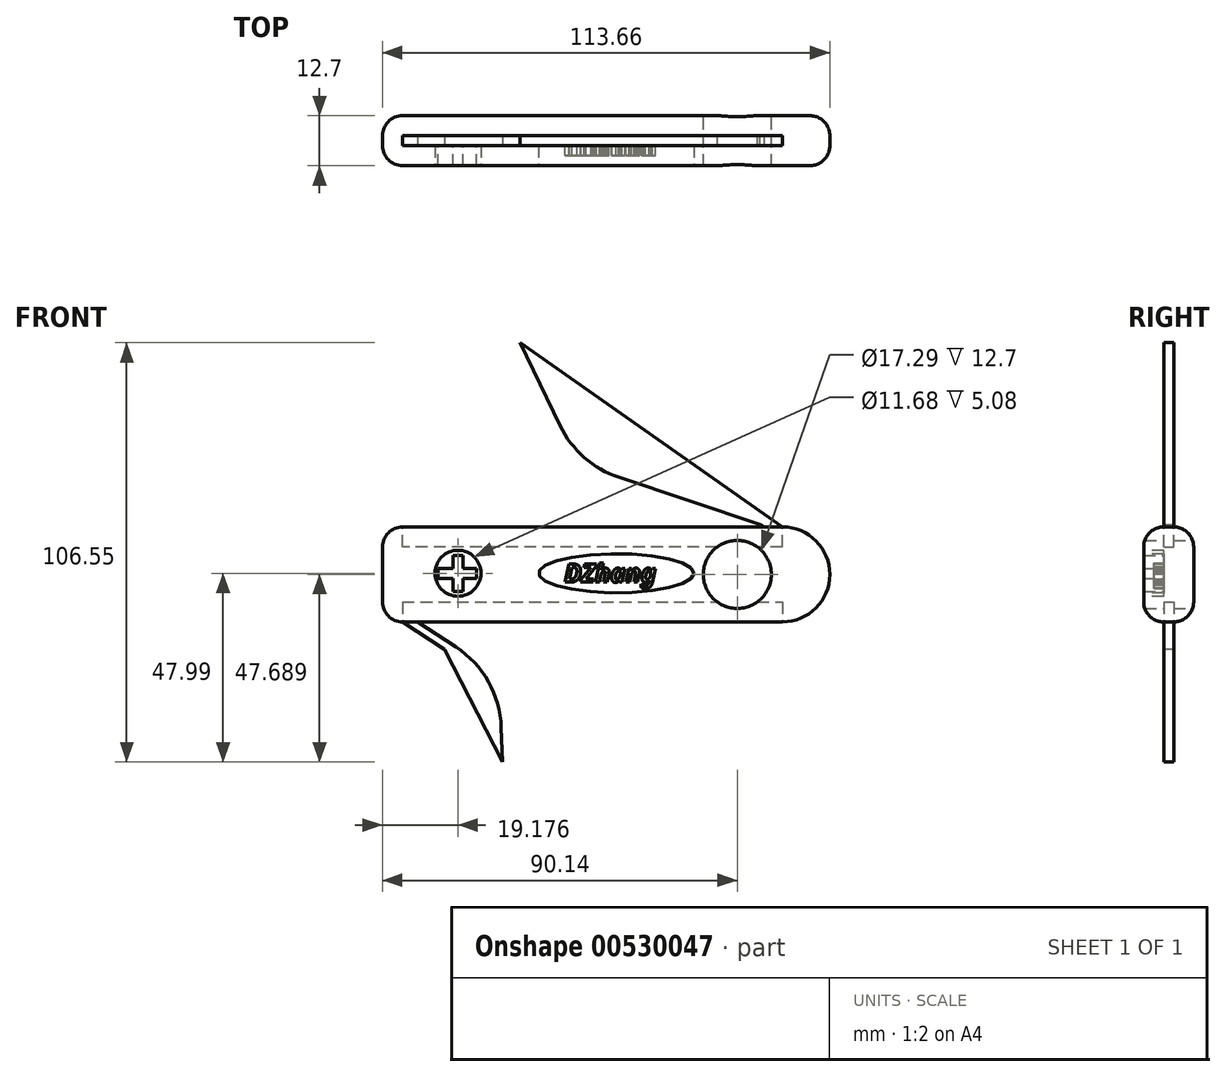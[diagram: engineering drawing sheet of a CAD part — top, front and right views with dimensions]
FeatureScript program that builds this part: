
annotation { "Feature Type Name" : "Feature", "Feature Type Description" : "" }
export const myFeature = defineFeature(function(context is Context, id is Id, definition is map)
    precondition{}
    {
        {
            var Q0;
            Q0=qCreatedBy(makeId("Front.planeOp"),FACE);
            var sketch = newSketch(context, id + "F0", { "sketchPlane" : qUnion([Q0])});
            skLineSegment(sketch, "E0", {"start": v(-34.28, 8.34) * mm, "end": v(23.42, 8.34) * mm});
            skLineSegment(sketch, "E1", {"start": v(23.42, 8.34) * mm, "end": v(23.42, -8.95) * mm, "construction": true});
            skLineSegment(sketch, "E2", {"start": v(23.42, -8.95) * mm, "end": v(-34.28, -8.95) * mm});
            skArc(sketch, "E3", {"start": v(23.42, -8.95) * mm, "mid": v(32.06, -0.3) * mm, "end": v(23.42, 8.34) * mm});
            skArc(sketch, "E4", {"start": v(23.42, 8.34) * mm, "mid": v(14.78, -0.3) * mm, "end": v(23.42, -8.95) * mm});
            skLineSegment(sketch, "E5", {"start": v(23.42, -8.95) * mm, "end": v(34.88, -8.95) * mm});
            skLineSegment(sketch, "E6", {"start": v(23.42, 8.34) * mm, "end": v(34.88, 8.34) * mm});
            skArc(sketch, "E7", {"start": v(34.88, -8.95) * mm, "mid": v(43.52, -0.3) * mm, "end": v(34.88, 8.34) * mm});
            skLineSegment(sketch, "E8", {"start": v(-66.72, -12.36) * mm, "end": v(34.88, -12.36) * mm});
            skLineSegment(sketch, "E9", {"start": v(34.88, -8.95) * mm, "end": v(34.88, -12.36) * mm, "construction": true});
            skLineSegment(sketch, "E10", {"start": v(34.88, 8.34) * mm, "end": v(34.88, 11.76) * mm, "construction": true});
            skLineSegment(sketch, "E11", {"start": v(34.88, 11.76) * mm, "end": v(-66.72, 11.76) * mm});
            skLineSegment(sketch, "E12", {"start": v(-66.72, -12.36) * mm, "end": v(-66.72, 11.76) * mm});
            skLineSegment(sketch, "E13", {"start": v(-34.28, -8.95) * mm, "end": v(-66.72, -8.95) * mm});
            skLineSegment(sketch, "E14", {"start": v(-34.28, 8.34) * mm, "end": v(-66.72, 8.34) * mm});
            skArc(sketch, "E15", {"start": v(34.88, -12.36) * mm, "mid": v(46.94, -0.3) * mm, "end": v(34.88, 11.76) * mm});
            skSolve(sketch);
        }
        {
            var Q0;
            {var subQ0=sQuery(id+"F0.wireOp",EDGE,"E0");Q0=makeQuery(id+"F0.imprint","IMPRINT",FACE,{"disambiguationData":[TD([[makeQuery(id+"F0.imprint","IMPRINT",EDGE,{"derivedFrom":subQ0}),-1.0]])]});}
            var Q1;
            {var subQ2=sQuery(id+"F0.wireOp",EDGE,"E0");Q1=makeQuery(id+"F0.imprint","IMPRINT",FACE,{"disambiguationData":[TD([[makeQuery(id+"F0.imprint","IMPRINT",EDGE,{"derivedFrom":subQ2}),1.0]])]});}
            var Q2;
            Q2=makeQuery(id+"F0.imprint","IMPRINT",FACE,{"disambiguationData":[TD([[makeQuery(id+"F0.imprint","IMPRINT",EDGE,{"derivedFrom":sQuery(id+"F0.wireOp",EDGE,"E3")}),-1.0]])]});
            extrude(context, id + "F1", {"entities" : qUnion([Q0, Q1, Q2]), "depth" : 12.7 * mm, "offsetDistance" : 25.4 * mm});
        }
        {
            var Q0;
            Q0=makeQuery(id+"F1.opExtrude","SWEPT_FACE",FACE,{"disambiguationData":[OSD([sQuery(id+"F0.wireOp",EDGE,"E8")])]});
            var Q1;
            Q1=makeQuery(id+"F1.opExtrude","SWEPT_FACE",FACE,{"disambiguationData":[OSD([sQuery(id+"F0.wireOp",EDGE,"E11")])]});
            fillet(context, id + "F2", {"entities" : qUnion([Q0, Q1]), "radius" : 5.08 * mm, "tangentPropagation" : true, "allowEdgeOverflow" : false});
        }
        {
            var Q0;
            Q0=makeQuery(id+"F1.opExtrude","SWEPT_FACE",FACE,{"disambiguationData":[OSD([sQuery(id+"F0.wireOp",EDGE,"E12")])]});
            fillet(context, id + "F3", {"entities" : qUnion([Q0]), "radius" : 5.08 * mm, "tangentPropagation" : true, "allowEdgeOverflow" : false});
        }
        {
            var Q0;
            Q0=makeQuery(id+"F1.opExtrude","SWEPT_FACE",FACE,{"disambiguationData":[OSD([sQuery(id+"F0.wireOp",EDGE,"E11")])]});
            extrude(context, id + "F4", {"entities" : qUnion([Q0]), "operationType" : NewBodyOperationType.REMOVE, "oppositeDirection" : true, "depth" : 5.08 * mm, "offsetDistance" : 25.4 * mm});
        }
        {
            var Q0;
            {var subQ0=sQuery(id+"F0.wireOp",EDGE,"E11");Q0=makeQuery(id+"F4.boolean.opBoolean","COPY",FACE,{"derivedFrom":makeQuery(id+"F4.opExtrude","SWEPT_FACE",FACE,{"disambiguationData":[OSD([subQ0]),TDD([makeQuery(id+"F2.opFillet","BLEND_EDGE",EDGE,{"blendedFrom":[makeQuery(id+"F1.opExtrude","CAP_EDGE",EDGE,{"disambiguationData":[OSD([subQ0])],"isStart":true}),makeQuery(id+"F1.opExtrude","SWEPT_FACE",FACE,{"disambiguationData":[OSD([subQ0])]})],"blendedInto":[makeQuery(id+"F1.opExtrude","SWEPT_FACE",FACE,{"disambiguationData":[OSD([subQ0])]})]})])]})});}
            var sketch = newSketch(context, id + "F5", { "sketchPlane" : qUnion([Q0])});
            skLineSegment(sketch, "E16", {"start": v(34.88, 11.76) * mm, "end": v(-31.74, 58.56) * mm});
            skLineSegment(sketch, "E17", {"start": v(-31.74, 58.56) * mm, "end": v(-21.58, 37.48) * mm});
            skLineSegment(sketch, "E18", {"start": v(34.88, 9.22) * mm, "end": v(29.21, 12.41) * mm});
            skPoint(sketch, "E19.visualSharp", {"position": v(-11.4, 16.33) * mm});
            skLineSegment(sketch, "E20", {"start": v(-6.74, 24.4) * mm, "end": v(29.21, 12.41) * mm});
            skPoint(sketch, "E21.visualSharp", {"position": v(-16.92, 27.8) * mm});
            skArc(sketch, "E21.filletArc", {"start": v(-21.58, 37.48) * mm, "mid": v(-15.48, 29.44) * mm, "end": v(-6.74, 24.4) * mm});
            skSolve(sketch);
        }
        {
            var Q0;
            {var subQ8=sQuery(id+"F5.wireOp",EDGE,"E16");Q0=makeQuery(id+"F5.imprint","IMPRINT",FACE,{"disambiguationData":[TD([[makeQuery(id+"F5.imprint","IMPRINT",EDGE,{"derivedFrom":subQ8}),1.0]])]});}
            extrude(context, id + "F6", {"entities" : qUnion([Q0]), "depth" : 2.54 * mm, "offsetDistance" : 25.4 * mm});
        }
        {
            var Q0;
            Q0=makeQuery(id+"F1.opExtrude","SWEPT_FACE",FACE,{"disambiguationData":[OSD([sQuery(id+"F0.wireOp",EDGE,"E8")])]});
            extrude(context, id + "F7", {"entities" : qUnion([Q0]), "operationType" : NewBodyOperationType.REMOVE, "oppositeDirection" : true, "depth" : 5.08 * mm, "offsetDistance" : 25.4 * mm});
        }
        {
            var Q0;
            Q0=makeQuery(id+"F2.opFillet","SPLIT",FACE,{"disambiguationData":[OD(1.0)],"derivedFrom":makeQuery(id+"F1.opExtrude","CAP_FACE",FACE,{"disambiguationData":[OSD([sQuery(id+"F0.wireOp",EDGE,"E3"),sQuery(id+"F0.wireOp",EDGE,"E4"),sQuery(id+"F0.wireOp",EDGE,"E8"),sQuery(id+"F0.wireOp",EDGE,"E11"),sQuery(id+"F0.wireOp",EDGE,"E12"),sQuery(id+"F0.wireOp",EDGE,"E15")])],"isStart":false})});
            var sketch = newSketch(context, id + "F8", { "sketchPlane" : qUnion([Q0])});
            skEllipse(sketch, "E22", {"center": v(-7.34, 0) * mm, "majorRadius": 19.7 * mm, "minorRadius": 4.96 * mm, "majorAxis": v(1, 0)});
            skCircle(sketch, "E23", {"center": v(-47.54, 0) * mm, "radius": 5.84 * mm});
            skSolve(sketch);
        }
        {
            var Q0;
            Q0=makeQuery(id+"F8.imprint","IMPRINT",FACE,{"disambiguationData":[TD([[makeQuery(id+"F8.imprint","IMPRINT",EDGE,{"derivedFrom":sQuery(id+"F8.wireOp",EDGE,"E22")}),1.0]])]});
            var Q1;
            Q1=makeQuery(id+"F8.imprint","IMPRINT",FACE,{"disambiguationData":[TD([[makeQuery(id+"F8.imprint","IMPRINT",EDGE,{"derivedFrom":sQuery(id+"F8.wireOp",EDGE,"E23")}),1.0]])]});
            extrude(context, id + "F9", {"entities" : qUnion([Q0, Q1]), "operationType" : NewBodyOperationType.REMOVE, "oppositeDirection" : true, "depth" : 5.08 * mm, "offsetDistance" : 25.4 * mm});
        }
        {
            var Q0;
            Q0=makeQuery(id+"F9.boolean.opBoolean","COPY",FACE,{"derivedFrom":makeQuery(id+"F9.opExtrude","CAP_FACE",FACE,{"disambiguationData":[OSD([sQuery(id+"F8.wireOp",EDGE,"E23")])],"isStart":false})});
            var sketch = newSketch(context, id + "F10", { "sketchPlane" : qUnion([Q0])});
            skLineSegment(sketch, "E24", {"start": v(-52.55, 0) * mm, "end": v(-52.55, -1.26) * mm});
            skLineSegment(sketch, "E25", {"start": v(-52.55, -1.26) * mm, "end": v(-42.86, -1.26) * mm});
            skLineSegment(sketch, "E26", {"start": v(-42.86, -1.26) * mm, "end": v(-42.86, 0) * mm});
            skLineSegment(sketch, "E27", {"start": v(-42.86, 0) * mm, "end": v(-42.86, 1.26) * mm});
            skLineSegment(sketch, "E28", {"start": v(-42.86, 1.26) * mm, "end": v(-52.55, 1.26) * mm});
            skLineSegment(sketch, "E29", {"start": v(-52.55, 1.26) * mm, "end": v(-52.55, 0) * mm});
            skLineSegment(sketch, "E30", {"start": v(-47.54, 4.56) * mm, "end": v(-46.28, 4.56) * mm});
            skLineSegment(sketch, "E31", {"start": v(-46.28, 4.56) * mm, "end": v(-46.28, 0) * mm});
            skLineSegment(sketch, "E32", {"start": v(-46.28, 0) * mm, "end": v(-46.28, -4.56) * mm});
            skLineSegment(sketch, "E33", {"start": v(-46.28, -4.56) * mm, "end": v(-47.54, -4.56) * mm});
            skLineSegment(sketch, "E34", {"start": v(-47.54, -4.56) * mm, "end": v(-48.8, -4.56) * mm});
            skLineSegment(sketch, "E35", {"start": v(-48.8, -4.56) * mm, "end": v(-48.8, 4.56) * mm});
            skLineSegment(sketch, "E36", {"start": v(-48.8, 4.56) * mm, "end": v(-47.54, 4.56) * mm});
            skSolve(sketch);
        }
        {
            var Q0;
            {var subQ4=sQuery(id+"F10.wireOp",EDGE,"E26");Q0=makeQuery(id+"F10.imprint","IMPRINT",FACE,{"disambiguationData":[TD([[makeQuery(id+"F10.imprint","IMPRINT",EDGE,{"derivedFrom":subQ4}),1.0]])]});}
            var Q1;
            {var subQ1=sQuery(id+"F10.wireOp",EDGE,"E33");Q1=makeQuery(id+"F10.imprint","IMPRINT",FACE,{"disambiguationData":[TD([[makeQuery(id+"F10.imprint","IMPRINT",EDGE,{"derivedFrom":subQ1}),-1.0]])]});}
            var Q2;
            {var subQ3=sQuery(id+"F10.wireOp",EDGE,"E25");var subQ5=sQuery(id+"F10.wireOp",EDGE,"E35");var subQ6=makeQuery(id+"F10.imprint","INTERSECT",VERTEX,{"derivedFrom":[subQ3,subQ5]});Q2=makeQuery(id+"F10.imprint","IMPRINT",FACE,{"disambiguationData":[TD([[makeQuery(id+"F10.imprint","IMPRINT",EDGE,{"disambiguationData":[TD([[subQ6,-1.0]])],"derivedFrom":subQ3}),1.0]])]});}
            var Q3;
            {var subQ5=sQuery(id+"F10.wireOp",EDGE,"E30");Q3=makeQuery(id+"F10.imprint","IMPRINT",FACE,{"disambiguationData":[TD([[makeQuery(id+"F10.imprint","IMPRINT",EDGE,{"derivedFrom":subQ5}),-1.0]])]});}
            var Q4;
            {var subQ5=sQuery(id+"F10.wireOp",EDGE,"E24");Q4=makeQuery(id+"F10.imprint","IMPRINT",FACE,{"disambiguationData":[TD([[makeQuery(id+"F10.imprint","IMPRINT",EDGE,{"derivedFrom":subQ5}),1.0]])]});}
            extrude(context, id + "F11", {"entities" : qUnion([Q0, Q1, Q2, Q3, Q4]), "operationType" : NewBodyOperationType.ADD, "depth" : 5.08 * mm, "offsetDistance" : 25.4 * mm});
        }
        {
            var Q0;
            Q0=makeQuery(id+"F9.boolean.opBoolean","COPY",FACE,{"derivedFrom":makeQuery(id+"F9.opExtrude","CAP_FACE",FACE,{"disambiguationData":[OSD([sQuery(id+"F8.wireOp",EDGE,"E22")])],"isStart":false})});
            var sketch = newSketch(context, id + "F12", { "sketchPlane" : qUnion([Q0])});
            skText(sketch, "E37", { "text": "DZhang", "fontName": "NotoSans-BoldItalic.ttf"});
            const initialGuessF12  = {"E37": [-0.02053, -0.00227, 1, 0, 0.00464]};
            skSetInitialGuess(sketch, initialGuessF12);
            skSolve(sketch);
        }
        {
            var Q0;
            {var subQ0=sQuery(id+"F0.wireOp",EDGE,"E8");Q0=makeQuery(id+"F7.boolean.opBoolean","COPY",FACE,{"derivedFrom":makeQuery(id+"F7.opExtrude","SWEPT_FACE",FACE,{"disambiguationData":[OSD([subQ0]),TDD([makeQuery(id+"F2.opFillet","BLEND_EDGE",EDGE,{"blendedFrom":[makeQuery(id+"F1.opExtrude","CAP_EDGE",EDGE,{"disambiguationData":[OSD([subQ0])],"isStart":false}),makeQuery(id+"F1.opExtrude","SWEPT_FACE",FACE,{"disambiguationData":[OSD([subQ0])]})],"blendedInto":[makeQuery(id+"F1.opExtrude","SWEPT_FACE",FACE,{"disambiguationData":[OSD([subQ0])]})]})])]})});}
            var sketch = newSketch(context, id + "F13", { "sketchPlane" : qUnion([Q0])});
            skPoint(sketch, "E38.visualSharp", {"position": v(35.06, 4.28) * mm});
            skLineSegment(sketch, "E39", {"start": v(61.64, -9.82) * mm, "end": v(48.03, -18.74) * mm});
            skLineSegment(sketch, "E40", {"start": v(61.64, -12.36) * mm, "end": v(51.02, -19.33) * mm});
            skLineSegment(sketch, "E41", {"start": v(36.57, -39.17) * mm, "end": v(36.29, -48) * mm});
            skLineSegment(sketch, "E42", {"start": v(36.29, -48) * mm, "end": v(51.02, -19.33) * mm});
            skPoint(sketch, "E43.visualSharp", {"position": v(37, -25.98) * mm});
            skArc(sketch, "E43.filletArc", {"start": v(48.03, -18.74) * mm, "mid": v(39.8, -27.56) * mm, "end": v(36.57, -39.17) * mm});
            skSolve(sketch);
        }
        {
            var Q0;
            {var subQ0=sQuery(id+"F13.wireOp",EDGE,"E40");Q0=makeQuery(id+"F13.imprint","IMPRINT",FACE,{"disambiguationData":[TD([[makeQuery(id+"F13.imprint","IMPRINT",EDGE,{"derivedFrom":subQ0}),-1.0]])]});}
            extrude(context, id + "F14", {"entities" : qUnion([Q0]), "depth" : 2.54 * mm, "offsetDistance" : 25.4 * mm});
        }
        {
            var Q0;
            Q0 = qSketchRegion(id + "F12", true);
            extrude(context, id + "F15", {"entities" : qUnion([Q0]), "operationType" : NewBodyOperationType.ADD, "depth" : 2.54 * mm, "offsetDistance" : 25.4 * mm});
        }
    });
